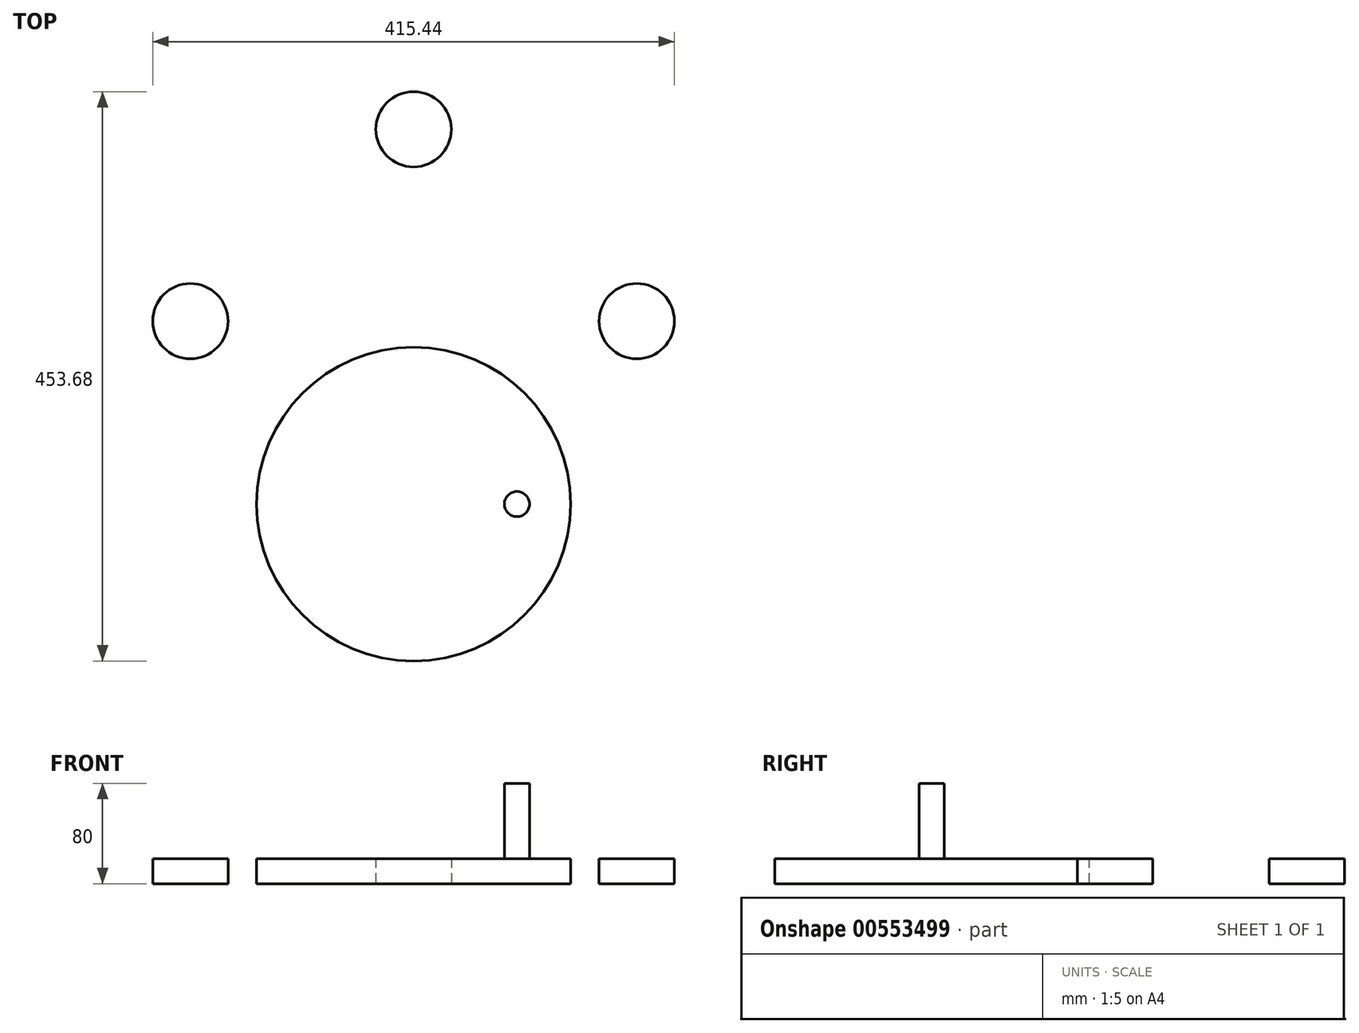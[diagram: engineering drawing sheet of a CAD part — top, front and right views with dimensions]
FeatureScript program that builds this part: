
annotation { "Feature Type Name" : "Feature", "Feature Type Description" : "" }
export const myFeature = defineFeature(function(context is Context, id is Id, definition is map)
    precondition{}
    {
        {
            var Q0;
            Q0=qCreatedBy(makeId("Top.planeOp"),FACE);
            var sketch = newSketch(context, id + "F0", { "sketchPlane" : qUnion([Q0])});
            skCircle(sketch, "E0", {"center": v(0, 0) * mm, "radius": 125 * mm});
            skLineSegment(sketch, "E1", {"start": v(0, 0) * mm, "end": v(0, 434.76) * mm, "construction": true});
            skCircle(sketch, "E2", {"center": v(177.72, 145.81) * mm, "radius": 30 * mm});
            skCircle(sketch, "E3.MirrorC", {"center": v(-177.72, 145.81) * mm, "radius": 30 * mm});
            skCircle(sketch, "E4", {"center": v(0, 298.68) * mm, "radius": 30 * mm});
            skSolve(sketch);
        }
        {
            var Q0;
            Q0=qSketchRegion(id+"F0",true);
            extrude(context, id + "F1", {"entities" : qUnion([Q0]), "depth" : 20 * mm});
        }
        {
            var Q0;
            Q0=makeQuery(id+"F1.opExtrude","CAP_FACE",FACE,{"disambiguationData":[OSD([sQuery(id+"F0.wireOp",EDGE,"E0")])],"isStart":false});
            var sketch = newSketch(context, id + "F2", { "sketchPlane" : qUnion([Q0])});
            skCircle(sketch, "E5", {"center": v(82.31, 0) * mm, "radius": 10 * mm});
            skSolve(sketch);
        }
        {
            var Q0;
            Q0 = qSketchRegion(id + "F2", true);
            extrude(context, id + "F3", {"entities" : qUnion([Q0]), "operationType" : NewBodyOperationType.ADD, "depth" : 60 * mm, "offsetDistance" : 25 * mm});
        }
    });
